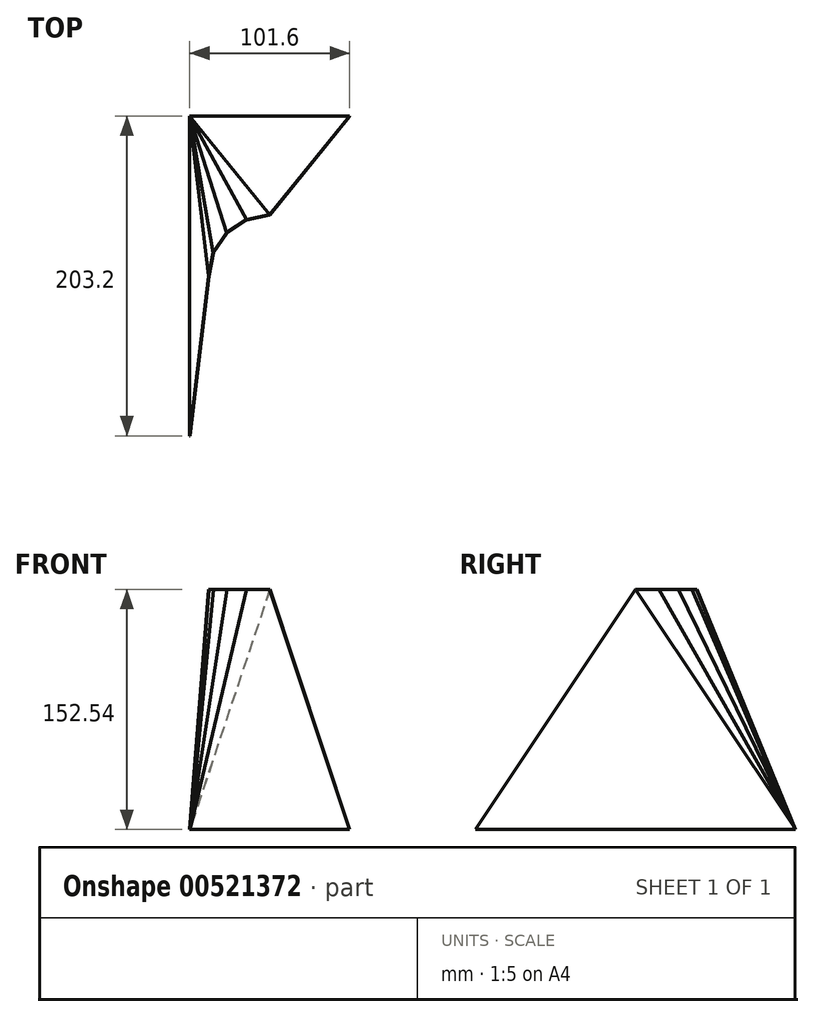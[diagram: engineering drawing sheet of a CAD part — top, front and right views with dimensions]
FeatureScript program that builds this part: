
annotation { "Feature Type Name" : "Feature", "Feature Type Description" : "" }
export const myFeature = defineFeature(function(context is Context, id is Id, definition is map)
    precondition{}
    {
        {
            var Q0;
            Q0=qCreatedBy(makeId("Top.planeOp"),FACE);
            var sketch = newSketch(context, id + "F0", { "sketchPlane" : qUnion([Q0])});
            skLineSegment(sketch, "E0.bottom", {"start": v(50.8, 101.6) * mm, "end": v(-50.8, 101.6) * mm});
            skLineSegment(sketch, "E0.top", {"start": v(50.8, -101.6) * mm, "end": v(-50.8, -101.6) * mm});
            skLineSegment(sketch, "E0.left", {"start": v(50.8, 101.6) * mm, "end": v(50.8, -101.6) * mm});
            skLineSegment(sketch, "E0.right", {"start": v(-50.8, 101.6) * mm, "end": v(-50.8, -101.6) * mm});
            skPoint(sketch, "E0.middle", {"position": v(0, 0) * mm});
            skSolve(sketch);
        }
        {
            var Q0;
            Q0=qCreatedBy(makeId("Top.planeOp"),FACE);
            cPlane(context, id + "F1", {"entities" : qUnion([Q0]), "cplaneType" : CPlaneType.OFFSET, "offset" : 152.4 * mm, "width" : 152.4 * mm, "height" : 152.4 * mm});
        }
        {
            var Q0;
            Q0=qCreatedBy(id+"F1.planeOp",FACE);
            var sketch = newSketch(context, id + "F2", { "sketchPlane" : qUnion([Q0])});
            skCircle(sketch, "E1.cCircle", {"center": v(0, 0) * mm, "radius": 38.1 * mm, "construction": true});
            skLineSegment(sketch, "E1.0", {"start": v(27.47, 27.47) * mm, "end": v(35.89, 14.87) * mm});
            skLineSegment(sketch, "E1.1", {"start": v(35.89, 14.87) * mm, "end": v(38.85, 0) * mm});
            skLineSegment(sketch, "E1.2", {"start": v(38.85, 0) * mm, "end": v(35.89, -14.87) * mm});
            skLineSegment(sketch, "E1.3", {"start": v(35.89, -14.87) * mm, "end": v(27.47, -27.47) * mm});
            skLineSegment(sketch, "E1.4", {"start": v(27.47, -27.47) * mm, "end": v(14.87, -35.89) * mm});
            skLineSegment(sketch, "E1.5", {"start": v(14.87, -35.89) * mm, "end": v(0, -38.85) * mm});
            skLineSegment(sketch, "E1.6", {"start": v(0, -38.85) * mm, "end": v(-14.87, -35.89) * mm});
            skLineSegment(sketch, "E1.7", {"start": v(-14.87, -35.89) * mm, "end": v(-27.47, -27.47) * mm});
            skLineSegment(sketch, "E1.8", {"start": v(-27.47, -27.47) * mm, "end": v(-35.89, -14.87) * mm});
            skLineSegment(sketch, "E1.9", {"start": v(-35.89, -14.87) * mm, "end": v(-38.85, 0) * mm});
            skLineSegment(sketch, "E1.10", {"start": v(-38.85, 0) * mm, "end": v(-35.89, 14.87) * mm});
            skLineSegment(sketch, "E1.11", {"start": v(-35.89, 14.87) * mm, "end": v(-27.47, 27.47) * mm});
            skLineSegment(sketch, "E1.12", {"start": v(-27.47, 27.47) * mm, "end": v(-14.87, 35.89) * mm});
            skLineSegment(sketch, "E1.13", {"start": v(-14.87, 35.89) * mm, "end": v(0, 38.85) * mm});
            skLineSegment(sketch, "E1.14", {"start": v(0, 38.85) * mm, "end": v(14.87, 35.89) * mm});
            skLineSegment(sketch, "E1.15", {"start": v(14.87, 35.89) * mm, "end": v(27.47, 27.47) * mm});
            skPoint(sketch, "E1.0.midPoint", {"position": v(31.68, 21.17) * mm});
            skSolve(sketch);
        }
        {
            var Q0;
            Q0=sQuery(id+"F2.wireOp",VERTEX,"E1.13.start");
            var Q1;
            Q1=sQuery(id+"F2.wireOp",VERTEX,"E1.12.start");
            var Q2;
            Q2=sQuery(id+"F0.wireOp",VERTEX,"E0.right.start");
            cPlane(context, id + "F3", {"entities" : qUnion([Q0, Q1, Q2]), "cplaneType" : CPlaneType.THREE_POINT, "offset" : 0 * mm, "width" : 152.4 * mm, "height" : 152.4 * mm});
        }
        {
            var Q0;
            Q0=qCreatedBy(id+"F3.planeOp",FACE);
            var sketch = newSketch(context, id + "F4", { "sketchPlane" : qUnion([Q0])});
            skLineSegment(sketch, "E2", {"start": v(-41.13, 113.12) * mm, "end": v(0.33, -51.54) * mm});
            skLineSegment(sketch, "E3", {"start": v(0.33, -51.54) * mm, "end": v(-26.59, 117.4) * mm});
            skLineSegment(sketch, "E4", {"start": v(-26.59, 117.4) * mm, "end": v(-41.13, 113.12) * mm});
            skSolve(sketch);
        }
        {
            var Q0;
            Q0=sQuery(id+"F2.wireOp",VERTEX,"E1.11.start");
            var Q1;
            Q1=sQuery(id+"F4.wireOp",VERTEX,"E3.start");
            var Q2;
            Q2=sQuery(id+"F4.wireOp",VERTEX,"E4.start");
            cPlane(context, id + "F5", {"entities" : qUnion([Q0, Q1, Q2]), "cplaneType" : CPlaneType.THREE_POINT, "offset" : 25.4 * mm, "width" : 152.4 * mm, "height" : 152.4 * mm});
        }
        {
            var Q0;
            Q0=qCreatedBy(id+"F5.planeOp",FACE);
            var sketch = newSketch(context, id + "F6", { "sketchPlane" : qUnion([Q0])});
            skLineSegment(sketch, "E5", {"start": v(23.2, 125.64) * mm, "end": v(-63.35, -21.91) * mm});
            skLineSegment(sketch, "E6", {"start": v(-63.35, -21.91) * mm, "end": v(37.92, 122.01) * mm});
            skLineSegment(sketch, "E7", {"start": v(37.92, 122.01) * mm, "end": v(23.2, 125.64) * mm});
            skSolve(sketch);
        }
        {
            var Q0;
            Q0=sQuery(id+"F6.wireOp",VERTEX,"E7.start");
            var Q1;
            Q1=sQuery(id+"F2.wireOp",VERTEX,"E1.10.start");
            var Q2;
            Q2=sQuery(id+"F4.wireOp",VERTEX,"E3.start");
            cPlane(context, id + "F7", {"entities" : qUnion([Q0, Q1, Q2]), "cplaneType" : CPlaneType.THREE_POINT, "offset" : 25.4 * mm, "width" : 152.4 * mm, "height" : 152.4 * mm});
        }
        {
            var Q0;
            Q0=qCreatedBy(id+"F7.planeOp",FACE);
            var sketch = newSketch(context, id + "F8", { "sketchPlane" : qUnion([Q0])});
            skLineSegment(sketch, "E8", {"start": v(-90.23, -10.49) * mm, "end": v(-1.87, 141.7) * mm});
            skLineSegment(sketch, "E9", {"start": v(-1.87, 141.7) * mm, "end": v(13.27, 141.1) * mm});
            skLineSegment(sketch, "E10", {"start": v(13.27, 141.1) * mm, "end": v(-90.23, -10.49) * mm});
            skSolve(sketch);
        }
        {
            var Q0;
            Q0=sQuery(id+"F4.wireOp",VERTEX,"E4.end");
            var Q1;
            Q1=sQuery(id+"F2.wireOp",VERTEX,"E1.14.start");
            var Q2;
            Q2=sQuery(id+"F8.wireOp",VERTEX,"E10.end");
            cPlane(context, id + "F9", {"entities" : qUnion([Q0, Q1, Q2]), "cplaneType" : CPlaneType.THREE_POINT, "offset" : 25.4 * mm, "width" : 152.4 * mm, "height" : 152.4 * mm});
        }
        {
            var Q0;
            Q0=qCreatedBy(id+"F9.planeOp",FACE);
            var sketch = newSketch(context, id + "F10", { "sketchPlane" : qUnion([Q0])});
            skLineSegment(sketch, "E11", {"start": v(-33.81, -43.82) * mm, "end": v(2.7, 122.02) * mm});
            skLineSegment(sketch, "E12", {"start": v(2.7, 122.02) * mm, "end": v(17.8, 120.74) * mm});
            skLineSegment(sketch, "E13", {"start": v(17.8, 120.74) * mm, "end": v(-33.81, -43.82) * mm});
            skSolve(sketch);
        }
        {
            var Q0;
            Q0=sQuery(id+"F10.wireOp",VERTEX,"E13.start");
            var Q1;
            Q1=sQuery(id+"F10.wireOp",VERTEX,"E11.start");
            var Q2;
            Q2=sQuery(id+"F0.wireOp",VERTEX,"E0.bottom.start");
            cPlane(context, id + "F11", {"entities" : qUnion([Q0, Q1, Q2]), "cplaneType" : CPlaneType.THREE_POINT, "offset" : 25.4 * mm, "width" : 152.4 * mm, "height" : 152.4 * mm});
        }
        {
            var Q0;
            Q0=qCreatedBy(id+"F11.planeOp",FACE);
            var sketch = newSketch(context, id + "F12", { "sketchPlane" : qUnion([Q0])});
            skLineSegment(sketch, "E14", {"start": v(0, 126.13) * mm, "end": v(50.8, -38.68) * mm});
            skLineSegment(sketch, "E15", {"start": v(50.8, -38.68) * mm, "end": v(-50.8, -38.68) * mm});
            skLineSegment(sketch, "E16", {"start": v(-50.8, -38.68) * mm, "end": v(0, 126.13) * mm});
            skSolve(sketch);
        }
        {
            var Q0;
            Q0=sQuery(id+"F8.wireOp",VERTEX,"E10.start");
            var Q1;
            Q1=sQuery(id+"F12.wireOp",VERTEX,"E15.start");
            var Q2;
            Q2=sQuery(id+"F0.wireOp",VERTEX,"E0.right.end");
            cPlane(context, id + "F13", {"entities" : qUnion([Q0, Q1, Q2]), "cplaneType" : CPlaneType.THREE_POINT, "offset" : 25.4 * mm, "width" : 152.4 * mm, "height" : 152.4 * mm});
        }
        {
            var Q0;
            Q0=qCreatedBy(id+"F13.planeOp",FACE);
            var sketch = newSketch(context, id + "F14", { "sketchPlane" : qUnion([Q0])});
            skLineSegment(sketch, "E17", {"start": v(101.6, -3.97) * mm, "end": v(0, 148.9) * mm});
            skLineSegment(sketch, "E18", {"start": v(0, 148.9) * mm, "end": v(-101.6, -3.97) * mm});
            skLineSegment(sketch, "E19", {"start": v(-101.6, -3.97) * mm, "end": v(101.6, -3.97) * mm});
            skSolve(sketch);
        }
        {
            var Q0;
            Q0 = qSketchRegion(id + "F14", true);
            extrude(context, id + "F15", {"entities" : qUnion([Q0]), "depth" : 0.32 * mm, "offsetDistance" : 25.4 * mm});
        }
        {
            var Q0;
            Q0 = qSketchRegion(id + "F8", true);
            extrude(context, id + "F16", {"entities" : qUnion([Q0]), "oppositeDirection" : true, "depth" : 0.32 * mm, "offsetDistance" : 25.4 * mm});
        }
        {
            var Q0;
            Q0 = qSketchRegion(id + "F6", true);
            extrude(context, id + "F17", {"entities" : qUnion([Q0]), "oppositeDirection" : true, "depth" : 0.32 * mm, "offsetDistance" : 25.4 * mm});
        }
        {
            var Q0;
            Q0 = qSketchRegion(id + "F4", true);
            extrude(context, id + "F18", {"entities" : qUnion([Q0]), "oppositeDirection" : true, "depth" : 0.32 * mm, "offsetDistance" : 25.4 * mm});
        }
        {
            var Q0;
            Q0 = qSketchRegion(id + "F10", true);
            extrude(context, id + "F19", {"entities" : qUnion([Q0]), "operationType" : NewBodyOperationType.ADD, "depth" : 0.32 * mm, "offsetDistance" : 25.4 * mm});
        }
        {
            var Q0;
            Q0 = qSketchRegion(id + "F12", true);
            extrude(context, id + "F20", {"entities" : qUnion([Q0]), "oppositeDirection" : true, "depth" : 0.32 * mm, "offsetDistance" : 25.4 * mm});
        }
    });
